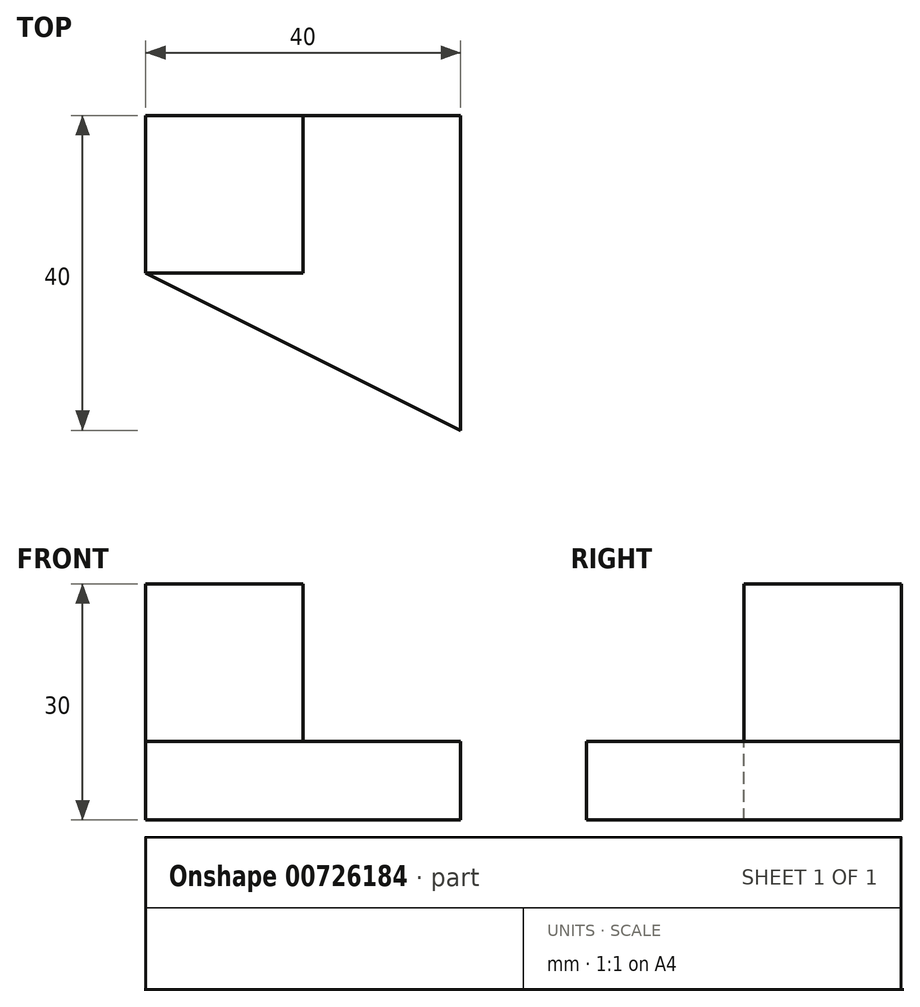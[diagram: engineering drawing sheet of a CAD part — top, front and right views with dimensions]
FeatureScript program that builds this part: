
annotation { "Feature Type Name" : "Feature", "Feature Type Description" : "" }
export const myFeature = defineFeature(function(context is Context, id is Id, definition is map)
    precondition{}
    {
        {
            var Q0;
            Q0=qCreatedBy(makeId("Front.planeOp"),FACE);
            var sketch = newSketch(context, id + "F0", { "sketchPlane" : qUnion([Q0])});
            skLineSegment(sketch, "E0", {"start": v(0, 0) * mm, "end": v(0, 30) * mm});
            skLineSegment(sketch, "E1", {"start": v(0, 30) * mm, "end": v(20, 30) * mm});
            skLineSegment(sketch, "E2", {"start": v(0, 0) * mm, "end": v(40, 0) * mm});
            skLineSegment(sketch, "E3", {"start": v(40, 0) * mm, "end": v(40, 10) * mm});
            skLineSegment(sketch, "E4", {"start": v(40, 10) * mm, "end": v(20, 10) * mm});
            skLineSegment(sketch, "E5", {"start": v(20, 10) * mm, "end": v(20, 30) * mm});
            skSolve(sketch);
        }
        {
            var Q0;
            Q0=makeQuery(id+"F0.imprint","IMPRINT",FACE,{"disambiguationData":[TD([[makeQuery(id+"F0.imprint","IMPRINT",EDGE,{"derivedFrom":sQuery(id+"F0.wireOp",EDGE,"E0")}),-1.0]])]});
            extrude(context, id + "F1", {"entities" : qUnion([Q0]), "depth" : 20 * mm, "offsetDistance" : 25 * mm});
        }
        {
            var Q0;
            Q0=makeQuery(id+"F1.opExtrude","CAP_FACE",FACE,{"disambiguationData":[OSD([sQuery(id+"F0.wireOp",EDGE,"E0"),sQuery(id+"F0.wireOp",EDGE,"E1"),sQuery(id+"F0.wireOp",EDGE,"E2"),sQuery(id+"F0.wireOp",EDGE,"E3"),sQuery(id+"F0.wireOp",EDGE,"E4"),sQuery(id+"F0.wireOp",EDGE,"E5")])],"isStart":false});
            var sketch = newSketch(context, id + "F2", { "sketchPlane" : qUnion([Q0])});
            skLineSegment(sketch, "E6", {"start": v(40, 10) * mm, "end": v(0, 10) * mm});
            skLineSegment(sketch, "E7", {"start": v(0, 10) * mm, "end": v(0, 0) * mm});
            skLineSegment(sketch, "E8", {"start": v(0, 0) * mm, "end": v(40, 0) * mm});
            skLineSegment(sketch, "E9", {"start": v(40, 0) * mm, "end": v(40, 10) * mm});
            skSolve(sketch);
        }
        {
            var Q0;
            Q0=qSketchRegion(id+"F2",true);
            extrude(context, id + "F3", {"entities" : qUnion([Q0]), "operationType" : NewBodyOperationType.ADD, "depth" : 20 * mm, "offsetDistance" : 25 * mm});
        }
        {
            var Q0;
            Q0=makeQuery(id+"F3.boolean.opBoolean","MERGE",FACE,{"derivedFrom":[makeQuery(id+"F1.opExtrude","SWEPT_FACE",FACE,{"disambiguationData":[OSD([sQuery(id+"F0.wireOp",EDGE,"E4")])]}),makeQuery(id+"F3.opExtrude","SWEPT_FACE",FACE,{"disambiguationData":[OSD([sQuery(id+"F2.wireOp",EDGE,"E6")])]})]});
            var sketch = newSketch(context, id + "F4", { "sketchPlane" : qUnion([Q0])});
            skLineSegment(sketch, "E10", {"start": v(0, -20) * mm, "end": v(40, -40) * mm});
            skLineSegment(sketch, "E11", {"start": v(40, -40) * mm, "end": v(0, -40) * mm});
            skLineSegment(sketch, "E12", {"start": v(0, -40) * mm, "end": v(0, -20) * mm});
            skSolve(sketch);
        }
        {
            var Q0;
            Q0=makeQuery(id+"F4.imprint","IMPRINT",FACE,{"disambiguationData":[TD([[makeQuery(id+"F4.imprint","IMPRINT",EDGE,{"derivedFrom":sQuery(id+"F4.wireOp",EDGE,"E10")}),-1.0]])]});
            extrude(context, id + "F5", {"entities" : qUnion([Q0]), "operationType" : NewBodyOperationType.REMOVE, "oppositeDirection" : true, "depth" : 10 * mm, "offsetDistance" : 25 * mm});
        }
    });
